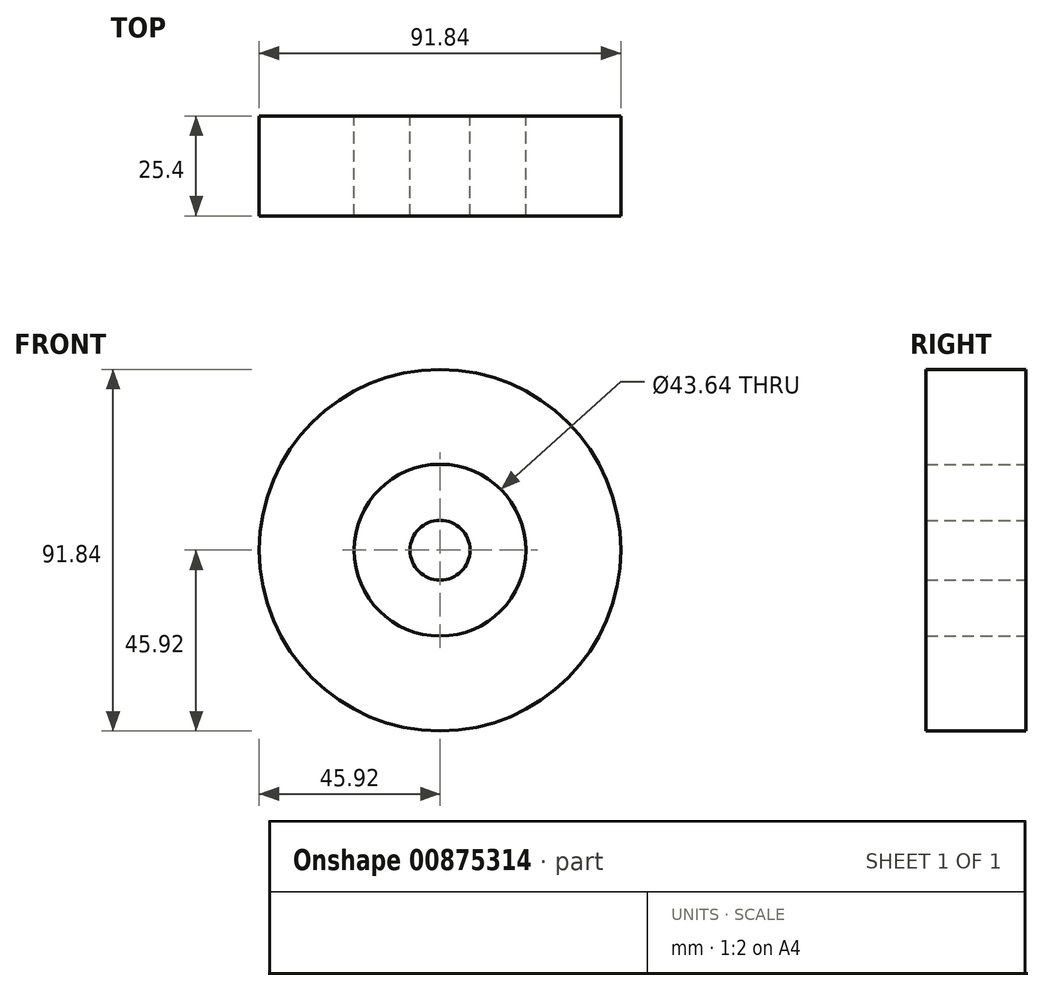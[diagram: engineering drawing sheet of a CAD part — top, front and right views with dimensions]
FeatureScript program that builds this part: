
annotation { "Feature Type Name" : "Feature", "Feature Type Description" : "" }
export const myFeature = defineFeature(function(context is Context, id is Id, definition is map)
    precondition{}
    {
        {
            var Q0;
            Q0=qCreatedBy(makeId("Front.planeOp"),FACE);
            var sketch = newSketch(context, id + "F0", { "sketchPlane" : qUnion([Q0])});
            skCircle(sketch, "E0", {"center": v(0, 0) * mm, "radius": 45.92 * mm});
            skCircle(sketch, "E1", {"center": v(0, 0) * mm, "radius": 21.82 * mm});
            skCircle(sketch, "E2", {"center": v(0, 0) * mm, "radius": 7.6 * mm});
            skSolve(sketch);
        }
        {
            var Q0;
            Q0=makeQuery(id+"F0.imprint","IMPRINT",FACE,{"disambiguationData":[TD([[makeQuery(id+"F0.imprint","IMPRINT",EDGE,{"derivedFrom":sQuery(id+"F0.wireOp",EDGE,"E0")}),1.0]])]});
            var Q1;
            Q1=makeQuery(id+"F0.imprint","IMPRINT",FACE,{"disambiguationData":[TD([[makeQuery(id+"F0.imprint","IMPRINT",EDGE,{"derivedFrom":sQuery(id+"F0.wireOp",EDGE,"E2")}),1.0]])]});
            extrude(context, id + "F1", {"entities" : qUnion([Q0, Q1]), "depth" : 25.4 * mm, "offsetDistance" : 25.4 * mm});
        }
    });
